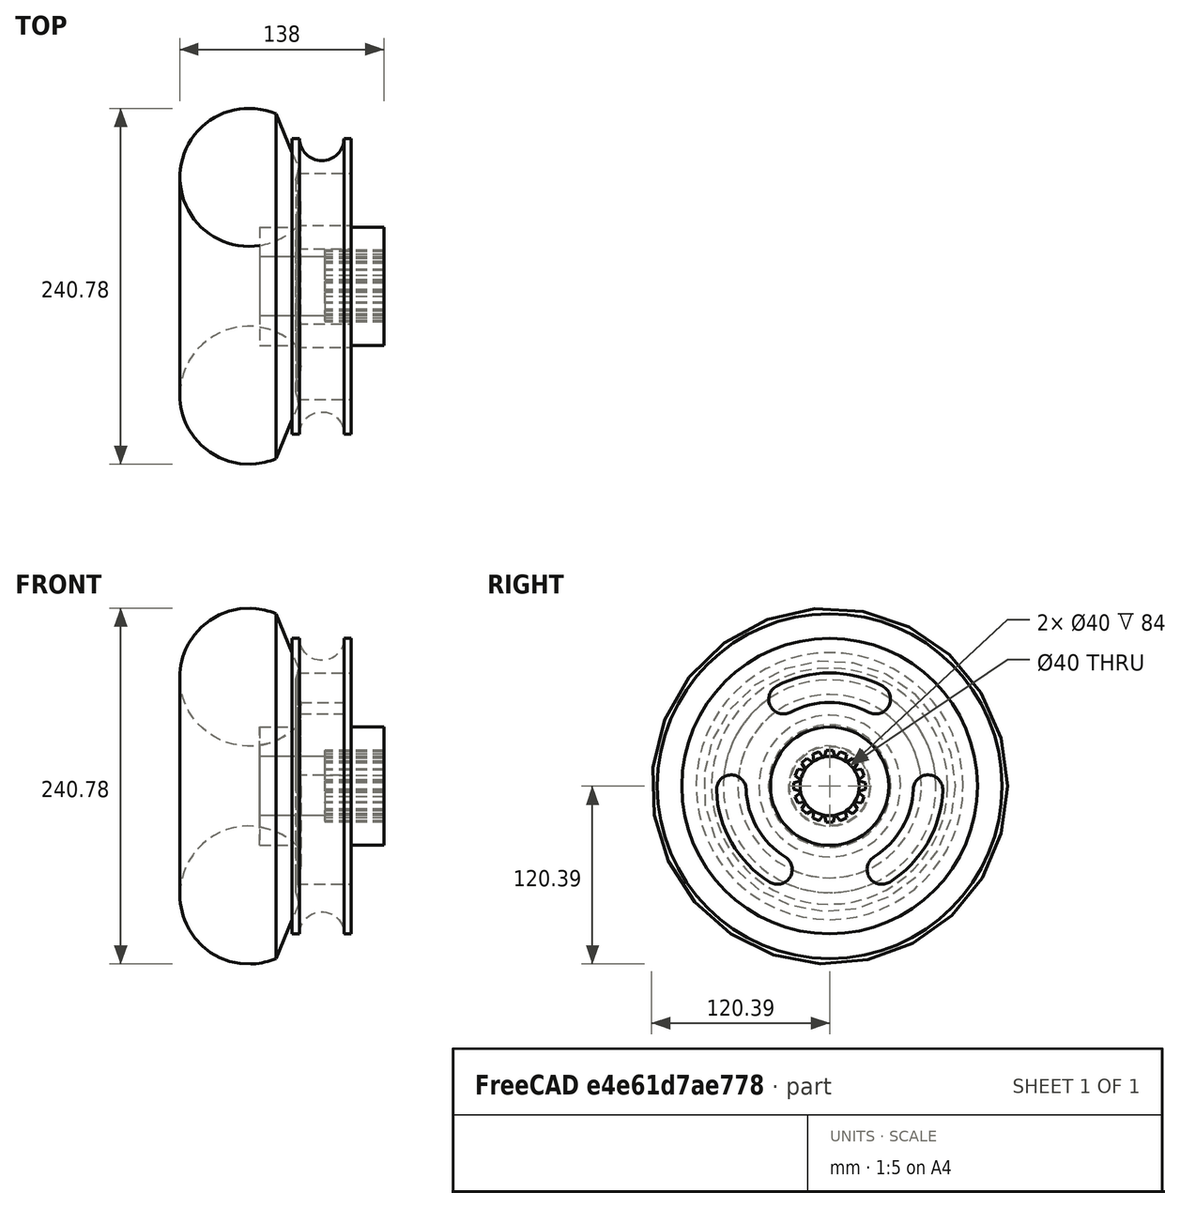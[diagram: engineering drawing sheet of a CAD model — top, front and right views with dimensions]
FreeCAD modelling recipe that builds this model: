
FCSTD DOCUMENT  (FreeCAD 0.18R4 (GitTag))
Label: test
License: All rights reserved
LicenseURL: http://en.wikipedia.org/wiki/All_rights_reserved
objects: Sketcher::SketchObject×5, PartDesign::Body×3, PartDesign::Revolution×2, PartDesign::Pocket×2, PartDesign::PolarPattern×2, Part::Cut×1, Mesh::Feature×1
note: 19 computed .brp shape members not serialized (recipe doc carries the construction recipe); baked Part::Feature solids carry a one-line shape summary decoded from their .brp

FEATURE [Sketcher::SketchObject] Sketch
  MapMode = 5
  Support = -> [XY_Plane]
  sketch-geometry (10):
    g0: LineSegment StartX=15 StartY=100 StartZ=0 EndX=20 EndY=100 EndZ=0
    g1: LineSegment StartX=20 StartY=100 StartZ=0 EndX=20 EndY=40 EndZ=0
    g2: LineSegment StartX=20 StartY=40 StartZ=0 EndX=42 EndY=40 EndZ=0
    g3: LineSegment StartX=42 StartY=40 StartZ=0 EndX=42 EndY=20 EndZ=0
    g4: LineSegment StartX=42 StartY=20 StartZ=0 EndX=-42 EndY=20 EndZ=0
    g5: LineSegment StartX=-42 StartY=20 StartZ=0 EndX=-42 EndY=40 EndZ=0
    g6: LineSegment StartX=-42 StartY=40 StartZ=0 EndX=-20 EndY=40 EndZ=0
    g7: LineSegment StartX=-20 StartY=40 StartZ=0 EndX=-20 EndY=100 EndZ=0
    g8: LineSegment StartX=-20 StartY=100 StartZ=0 EndX=-15 EndY=100 EndZ=0
    g9: ArcOfCircle CenterX=-9e-16 CenterY=100 CenterZ=0 NormalX=0 NormalY=0 NormalZ=1 AngleXU=0 Radius=15 StartAngle=3.14159 EndAngle=6.28319
  constraints (28):
    c: Coincident(g0,g1)
    c: Vertical(g1)
    c: Coincident(g1,g2)
    c: Coincident(g2,g3)
    c: Vertical(g3)
    c: Coincident(g3,g4)
    c: Horizontal(g4)
    c: Coincident(g4,g5)
    c: Coincident(g5,g6)
    c: Coincident(g6,g7)
    c: Coincident(g7,g8)
    c: Horizontal(g2)
    c: Vertical(g7)
    c: Vertical(g5)
    c: Horizontal(g8)
    c: Horizontal(g6)
    c: Coincident(g9,g0)
    c: Coincident(g9,g8)
    c: DistanceY(g3) = 20
    c: DistanceY(g2) = 40
    c: Symmetric(g0,g7,g-2)
    c: Symmetric(g2,g5,g-2)
    c: Radius(g9) = 15
    c: Symmetric(g8,g0,g-2)
    c: Perpendicular(g9,g8)
    c: DistanceX(g7) = -20
    c: DistanceY(g7) = 100
    c: DistanceX(g6,g6) = 22
FEATURE [PartDesign::Revolution] Revolution
  Angle = 360
  Axis = (1,0,0)
  Base = (0,0,0)
  Profile = -> Sketch
  ReferenceAxis = -> Sketch [H_Axis]
FEATURE [Sketcher::SketchObject] Sketch001
  MapMode = 5
  Support = -> [XY_Plane001]
  sketch-geometry (6):
    g0: ArcOfCircle CenterX=-57.5551 CenterY=86.7057 CenterZ=0 NormalX=0 NormalY=0 NormalZ=1 AngleXU=0 Radius=42.4452 StartAngle=5.92879 EndAngle=6.12303
    g1: ArcOfCircle CenterX=58.1424 CenterY=72.0139 CenterZ=0 NormalX=0 NormalY=0 NormalZ=1 AngleXU=0 Radius=75.8899 StartAngle=3.14209 EndAngle=3.27335
    g2: ArcOfCircle CenterX=-25.2553 CenterY=54.6035 CenterZ=0 NormalX=0 NormalY=0 NormalZ=1 AngleXU=0 Radius=11.047 StartAngle=5.63299 EndAngle=7.02217
    g3: ArcOfCircle CenterX=24.1007 CenterY=49.944 CenterZ=0 NormalX=0 NormalY=0 NormalZ=1 AngleXU=0 Radius=40.6136 StartAngle=3.19154 EndAngle=3.35221
    g4: ArcOfCircle CenterX=-49.334 CenterY=73.7202 CenterZ=0 NormalX=0 NormalY=0 NormalZ=1 AngleXU=0 Radius=46.67 StartAngle=1.16868 EndAngle=5.51978
    g5: LineSegment StartX=-31.0689 StartY=116.668 StartZ=0 EndX=-15.6531 EndY=79.9369 EndZ=0
  constraints (23):
    c: Coincident(g1,g0)
    c: Coincident(g2,g1)
    c: Coincident(g3,g2)
    c: Coincident(g4,g3)
    c: Coincident(g5,g4)
    c: Coincident(g5,g0)
    c: DistanceX(g2,g0) = 0.809153
    c: DistanceY(g2,g0) = 32.0207
    c: DistanceX(g1,g0) = 1.43672
    c: DistanceY(g1,g0) = 17.8929
    c: DistanceX(g0,g0) = 2.09444
    c: DistanceY(g0,g0) = 7.96052
    c: DistanceX(g4,g2) = 14.6067
    c: DistanceY(g4,g2) = -68.7513
    c: DistanceX(g3,g2) = -0.846787
    c: DistanceY(g3,g2) = 6.46293
    c: DistanceX(g4) = -31.0689
    c: DistanceY(g4) = 116.668
    c: Radius(g4) = 46.67
    c: DistanceX(g1,g0) = -115.697
    c: DistanceY(g1,g0) = 14.6918
    c: DistanceX(g3,g0) = -81.6557
    c: DistanceX(g2) = -25.2553
FEATURE [PartDesign::Revolution] Revolution001
  Angle = 360
  Axis = (1,0,0)
  Base = (0,0,0)
  Profile = -> Sketch001
  ReferenceAxis = -> Sketch001 [H_Axis]
FEATURE [Part::Cut] Cut
  Base = -> Revolution
  Tool = -> Revolution001
FEATURE [Sketcher::SketchObject] Sketch002
  MapMode = 5
  Placement = pos=(20,0,0) rot=(0.57735,0.57735,0.57735;2.0944rad)
  Support = -> [Cut]
  sketch-geometry (4):
    g0: ArcOfCircle CenterX=-31.1943 CenterY=58.835 CenterZ=0 NormalX=0 NormalY=0 NormalZ=1 AngleXU=0 Radius=10 StartAngle=2.05831 EndAngle=5.1999
    g1: ArcOfCircle CenterX=31.1943 CenterY=58.835 CenterZ=0 NormalX=0 NormalY=0 NormalZ=1 AngleXU=0 Radius=10 StartAngle=4.22487 EndAngle=7.36647
    g2: ArcOfCircle CenterX=-1.7763e-12 CenterY=0 CenterZ=0 NormalX=0 NormalY=0 NormalZ=1 AngleXU=0 Radius=56.5931 StartAngle=1.08328 EndAngle=2.05831
    g3: ArcOfCircle CenterX=-1.7763e-12 CenterY=0 CenterZ=0 NormalX=0 NormalY=0 NormalZ=1 AngleXU=0 Radius=76.5931 StartAngle=1.08328 EndAngle=2.05831
  constraints (11):
    c: Coincident(g2,g-1)
    c: Coincident(g3,g2)
    c: Radius(g1) = 10
    c: Tangent(g3,g1) = -1.5708
    c: Tangent(g2,g1) = 1.5708
    c: Tangent(g0,g2) = 1.5708
    c: Tangent(g0,g3) = -1.5708
    c: Symmetric(g0,g1,g-2)
    c: Symmetric(g1,g0,g-2)
    c: DistanceY(g1) = 50
    c: DistanceY(g0) = 67.67
FEATURE [PartDesign::Body] Body001
  Group = -> [Sketch001,Revolution001]
  Origin = -> Origin001
  Tip = -> Revolution001
FEATURE [PartDesign::Pocket] Pocket
  Length = 5
  Length2 = 100
  Profile = -> Sketch002
  Type = 1
FEATURE [PartDesign::PolarPattern] PolarPattern
  Angle = 360
  Axis = -> Sketch002 [N_Axis]
  BaseFeature = -> Pocket
  Occurrences = 3
  Originals = -> [Pocket]
FEATURE [Sketcher::SketchObject] Sketch003
  MapMode = 5
  Placement = pos=(0,0,0) rot=(0.57735,0.57735,0.57735;2.0944rad)
  Support = -> [YZ_Plane]
FEATURE [PartDesign::Body] Body
  Group = -> [Sketch,Revolution,Sketch003]
  Origin = -> Origin
  Tip = -> Revolution
FEATURE [Sketcher::SketchObject] Sketch004
  MapMode = 5
  Placement = pos=(42,0,0) rot=(0.57735,0.57735,0.57735;2.0944rad)
  Support = -> [PolarPattern]
  sketch-geometry (4):
    g0: LineSegment StartX=-2.29 StartY=24.3 StartZ=0 EndX=-4.36 EndY=16.1 EndZ=0
    g1: LineSegment StartX=-4.36 StartY=16.1 StartZ=0 EndX=4.36 EndY=16.1 EndZ=0
    g2: LineSegment StartX=4.36 StartY=16.1 StartZ=0 EndX=2.29 EndY=24.3 EndZ=0
    g3: LineSegment StartX=2.29 StartY=24.3 StartZ=0 EndX=-2.29 EndY=24.3 EndZ=0
  constraints (10):
    c: Coincident(g0,g1)
    c: Coincident(g1,g2)
    c: Coincident(g2,g3)
    c: Coincident(g3,g0)
    c: Symmetric(g0,g2,g-2)
    c: Symmetric(g1,g0,g-2)
    c: DistanceY(g2) = 24.3
    c: DistanceY(g1) = 16.1
    c: DistanceX(g2) = 2.29
    c: DistanceX(g1) = 4.36
FEATURE [PartDesign::Pocket] Pocket001
  BaseFeature = -> PolarPattern
  Length = 40
  Length2 = 100
  Profile = -> Sketch004
  Type = 0
FEATURE [PartDesign::PolarPattern] PolarPattern001
  Angle = 360
  Axis = -> Sketch004 [N_Axis]
  BaseFeature = -> Pocket001
  Occurrences = 16
  Originals = -> [Pocket001]
FEATURE [PartDesign::Body] Body002
  Group = -> [Sketch002,Pocket,PolarPattern,Sketch004,Pocket001,PolarPattern001]
  Origin = -> Origin002
  Tip = -> PolarPattern001
FEATURE [Mesh::Feature] test
